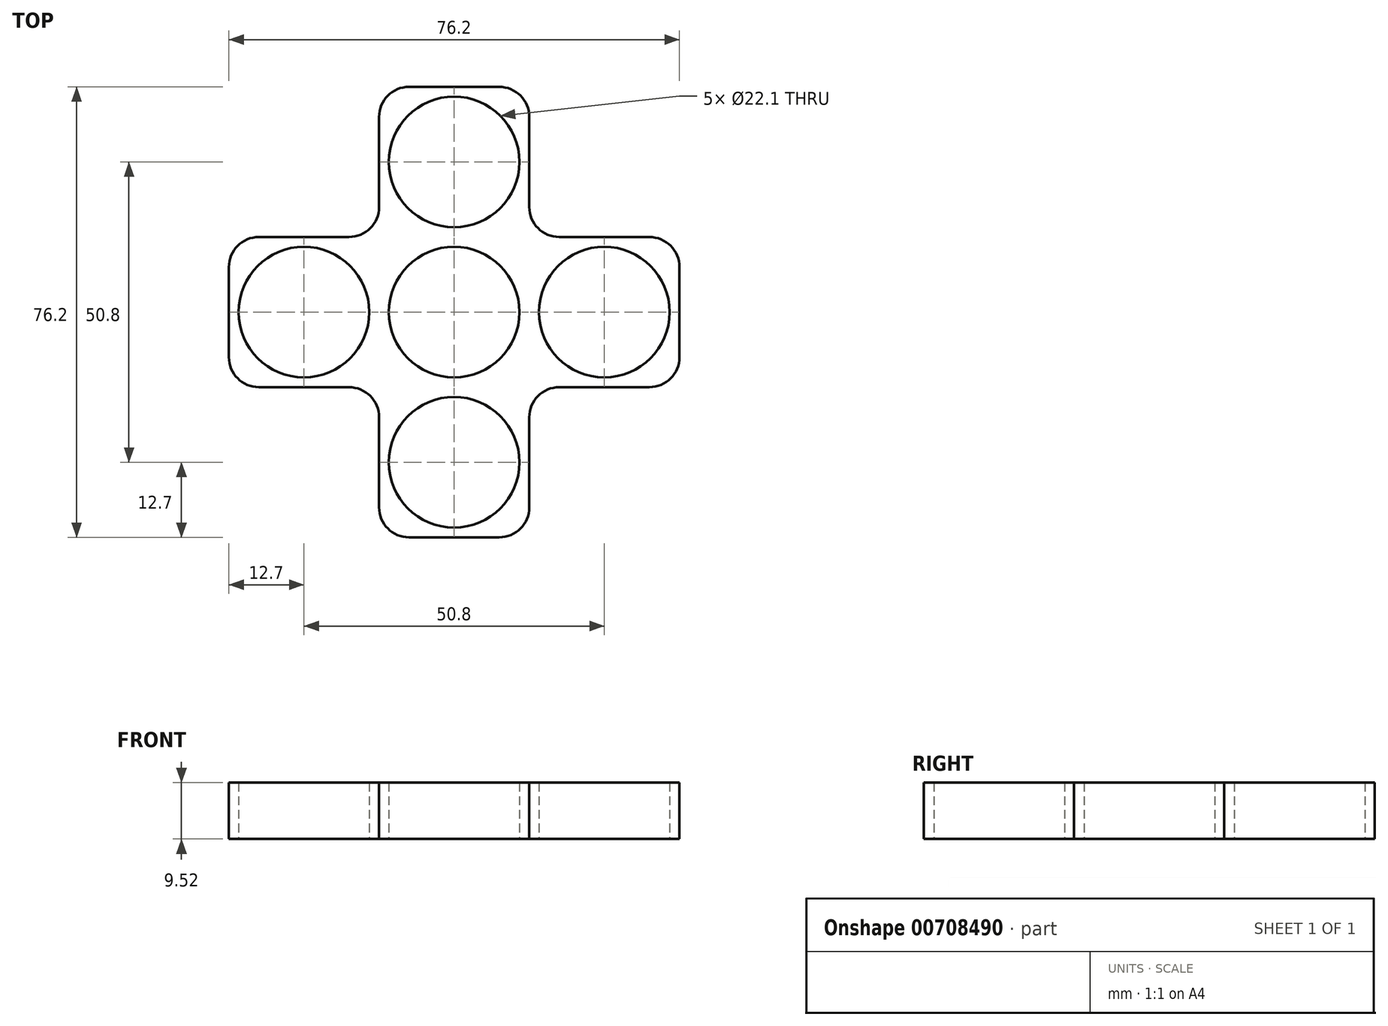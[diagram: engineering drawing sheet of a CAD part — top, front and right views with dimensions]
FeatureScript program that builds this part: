
annotation { "Feature Type Name" : "Feature", "Feature Type Description" : "" }
export const myFeature = defineFeature(function(context is Context, id is Id, definition is map)
    precondition{}
    {
        {
            var Q0;
            Q0=qCreatedBy(makeId("Top.planeOp"),FACE);
            var sketch = newSketch(context, id + "F0", { "sketchPlane" : qUnion([Q0])});
            skCircle(sketch, "E0", {"center": v(0, 0) * mm, "radius": 12.7 * mm});
            skCircle(sketch, "E1", {"center": v(0, 0) * mm, "radius": 11.05 * mm});
            skSolve(sketch);
        }
        {
            var Q0;
            Q0=makeQuery(id+"F0.imprint","IMPRINT",FACE,{"disambiguationData":[TD([[makeQuery(id+"F0.imprint","IMPRINT",EDGE,{"derivedFrom":sQuery(id+"F0.wireOp",EDGE,"E0")}),1.0]])]});
            extrude(context, id + "F1", {"entities" : qUnion([Q0]), "endBound" : BoundingType.SYMMETRIC, "depth" : 9.52 * mm, "offsetDistance" : 25.4 * mm});
        }
        {
            var Q0;
            Q0=qCreatedBy(makeId("Top.planeOp"),FACE);
            var sketch = newSketch(context, id + "F2", { "sketchPlane" : qUnion([Q0])});
            skLineSegment(sketch, "E2.bottom", {"start": v(-12.7, 38.1) * mm, "end": v(12.7, 38.1) * mm});
            skLineSegment(sketch, "E2.top", {"start": v(-12.7, -38.1) * mm, "end": v(12.7, -38.1) * mm});
            skLineSegment(sketch, "E2.left", {"start": v(-12.7, 38.1) * mm, "end": v(-12.7, 12.7) * mm});
            skLineSegment(sketch, "E2.right", {"start": v(12.7, 38.1) * mm, "end": v(12.7, 12.7) * mm});
            skPoint(sketch, "E2.middle", {"position": v(0, 0) * mm});
            skLineSegment(sketch, "E3", {"start": v(0, 0) * mm, "end": v(0, 25.4) * mm});
            skLineSegment(sketch, "E4", {"start": v(0, 0) * mm, "end": v(0, -25.4) * mm});
            skLineSegment(sketch, "E5", {"start": v(0, 0) * mm, "end": v(-25.4, 0) * mm});
            skLineSegment(sketch, "E6", {"start": v(0, 0) * mm, "end": v(25.4, 0) * mm});
            skCircle(sketch, "E7", {"center": v(-25.4, 0) * mm, "radius": 12.7 * mm});
            skCircle(sketch, "E8", {"center": v(-25.4, 0) * mm, "radius": 11.05 * mm});
            skCircle(sketch, "E9", {"center": v(0, -25.4) * mm, "radius": 12.7 * mm});
            skCircle(sketch, "E10", {"center": v(0, -25.4) * mm, "radius": 11.05 * mm});
            skCircle(sketch, "E11", {"center": v(25.4, 0) * mm, "radius": 12.7 * mm});
            skCircle(sketch, "E12", {"center": v(25.4, 0) * mm, "radius": 11.05 * mm});
            skCircle(sketch, "E13", {"center": v(0, 25.4) * mm, "radius": 12.7 * mm});
            skCircle(sketch, "E14", {"center": v(0, 25.4) * mm, "radius": 11.05 * mm});
            skLineSegment(sketch, "E15.bottom", {"start": v(-38.1, 12.7) * mm, "end": v(-12.7, 12.7) * mm});
            skLineSegment(sketch, "E15.top", {"start": v(-38.1, -12.7) * mm, "end": v(-12.7, -12.7) * mm});
            skLineSegment(sketch, "E15.left", {"start": v(-38.1, 12.7) * mm, "end": v(-38.1, -12.7) * mm});
            skLineSegment(sketch, "E15.right", {"start": v(38.1, 12.7) * mm, "end": v(38.1, -12.7) * mm});
            skLineSegment(sketch, "E16.trimOffspring", {"start": v(12.7, 12.7) * mm, "end": v(38.1, 12.7) * mm});
            skLineSegment(sketch, "E17.trimOffspring", {"start": v(-12.7, -12.7) * mm, "end": v(-12.7, -38.1) * mm});
            skLineSegment(sketch, "E18.trimOffspring", {"start": v(12.7, -12.7) * mm, "end": v(38.1, -12.7) * mm});
            skLineSegment(sketch, "E19.trimOffspring", {"start": v(12.7, -12.7) * mm, "end": v(12.7, -38.1) * mm});
            skCircle(sketch, "E20", {"center": v(0, 0) * mm, "radius": 12.7 * mm});
            skCircle(sketch, "E21", {"center": v(0, 0) * mm, "radius": 11.05 * mm});
            skSolve(sketch);
        }
        {
            var Q0;
            Q0 = qSketchRegion(id + "F2", true);
            extrude(context, id + "F3", {"entities" : qUnion([Q0]), "operationType" : NewBodyOperationType.ADD, "endBound" : BoundingType.SYMMETRIC, "depth" : 9.52 * mm, "offsetDistance" : 25.4 * mm});
        }
        {
            var Q0;
            Q0=makeQuery(id+"F3.opExtrude","SWEPT_EDGE",EDGE,{"disambiguationData":[OSD([sQuery(id+"F2.wireOp",EDGE,"E18.trimOffspring"),sQuery(id+"F2.wireOp",EDGE,"E19.trimOffspring")])]});
            var Q1;
            Q1=makeQuery(id+"F3.opExtrude","SWEPT_EDGE",EDGE,{"disambiguationData":[OSD([sQuery(id+"F2.wireOp",EDGE,"E2.top"),sQuery(id+"F2.wireOp",EDGE,"E19.trimOffspring")])]});
            var Q2;
            Q2=makeQuery(id+"F3.opExtrude","SWEPT_EDGE",EDGE,{"disambiguationData":[OSD([sQuery(id+"F2.wireOp",EDGE,"E2.top"),sQuery(id+"F2.wireOp",EDGE,"E17.trimOffspring")])]});
            var Q3;
            Q3=makeQuery(id+"F3.opExtrude","SWEPT_EDGE",EDGE,{"disambiguationData":[OSD([sQuery(id+"F2.wireOp",EDGE,"E15.right"),sQuery(id+"F2.wireOp",EDGE,"E18.trimOffspring")])]});
            var Q4;
            Q4=makeQuery(id+"F3.opExtrude","SWEPT_EDGE",EDGE,{"disambiguationData":[OSD([sQuery(id+"F2.wireOp",EDGE,"E15.right"),sQuery(id+"F2.wireOp",EDGE,"E16.trimOffspring")])]});
            var Q5;
            Q5=makeQuery(id+"F3.opExtrude","SWEPT_EDGE",EDGE,{"disambiguationData":[OSD([sQuery(id+"F2.wireOp",EDGE,"E2.bottom"),sQuery(id+"F2.wireOp",EDGE,"E2.right")])]});
            var Q6;
            Q6=makeQuery(id+"F3.opExtrude","SWEPT_EDGE",EDGE,{"disambiguationData":[OSD([sQuery(id+"F2.wireOp",EDGE,"E15.bottom"),sQuery(id+"F2.wireOp",EDGE,"E15.left")])]});
            var Q7;
            Q7=makeQuery(id+"F3.opExtrude","SWEPT_EDGE",EDGE,{"disambiguationData":[OSD([sQuery(id+"F2.wireOp",EDGE,"E2.bottom"),sQuery(id+"F2.wireOp",EDGE,"E2.left")])]});
            var Q8;
            Q8=makeQuery(id+"F3.opExtrude","SWEPT_EDGE",EDGE,{"disambiguationData":[OSD([sQuery(id+"F2.wireOp",EDGE,"E2.right"),sQuery(id+"F2.wireOp",EDGE,"E16.trimOffspring")])]});
            var Q9;
            Q9=makeQuery(id+"F3.opExtrude","SWEPT_EDGE",EDGE,{"disambiguationData":[OSD([sQuery(id+"F2.wireOp",EDGE,"E2.left"),sQuery(id+"F2.wireOp",EDGE,"E15.bottom")])]});
            var Q10;
            Q10=makeQuery(id+"F3.opExtrude","SWEPT_EDGE",EDGE,{"disambiguationData":[OSD([sQuery(id+"F2.wireOp",EDGE,"E15.top"),sQuery(id+"F2.wireOp",EDGE,"E15.left")])]});
            var Q11;
            Q11=makeQuery(id+"F3.opExtrude","SWEPT_EDGE",EDGE,{"disambiguationData":[OSD([sQuery(id+"F2.wireOp",EDGE,"E15.top"),sQuery(id+"F2.wireOp",EDGE,"E17.trimOffspring")])]});
            fillet(context, id + "F4", {"entities" : qUnion([Q0, Q1, Q2, Q3, Q4, Q5, Q6, Q7, Q8, Q9, Q10, Q11]), "radius" : 5.08 * mm, "tangentPropagation" : true, "allowEdgeOverflow" : false});
        }
    });
